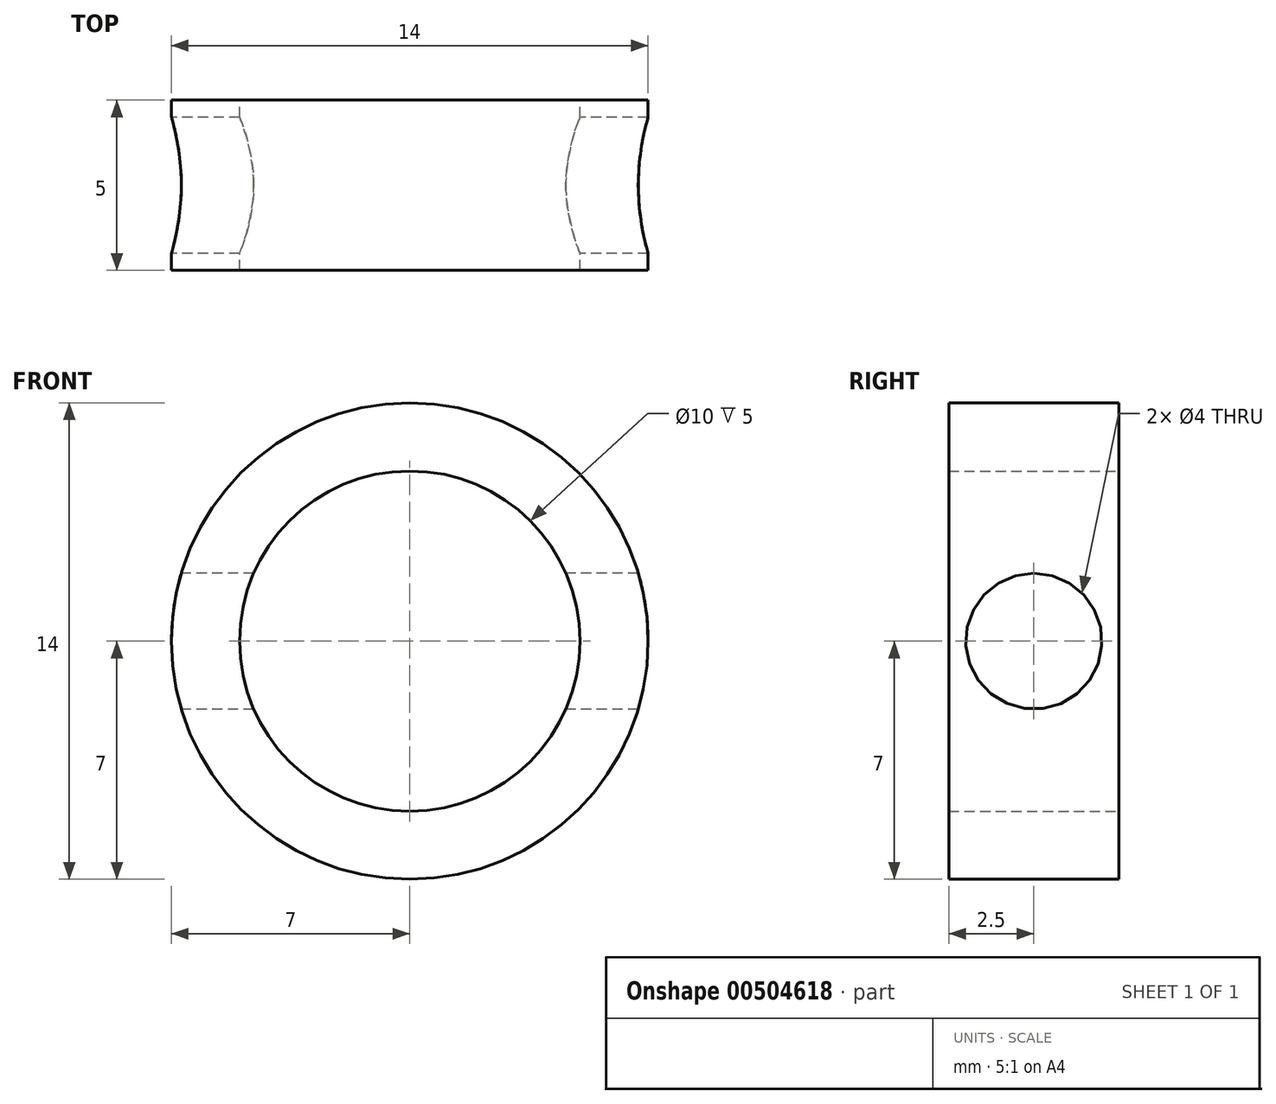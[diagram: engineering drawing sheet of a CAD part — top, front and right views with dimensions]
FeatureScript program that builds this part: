
annotation { "Feature Type Name" : "Feature", "Feature Type Description" : "" }
export const myFeature = defineFeature(function(context is Context, id is Id, definition is map)
    precondition{}
    {
        {
            var Q0;
            Q0=qCreatedBy(makeId("Front.planeOp"),FACE);
            var sketch = newSketch(context, id + "F0", { "sketchPlane" : qUnion([Q0])});
            skCircle(sketch, "E0", {"center": v(0, 0) * mm, "radius": 5 * mm});
            skCircle(sketch, "E1", {"center": v(0, 0) * mm, "radius": 7 * mm});
            skSolve(sketch);
        }
        {
            var Q0;
            Q0 = qSketchRegion(id + "F0", true);
            extrude(context, id + "F1", {"entities" : qUnion([Q0]), "depth" : 5 * mm, "offsetDistance" : 25 * mm});
        }
        {
            var Q0;
            Q0=qCreatedBy(makeId("Right.planeOp"),FACE);
            var sketch = newSketch(context, id + "F2", { "sketchPlane" : qUnion([Q0])});
            skCircle(sketch, "E2", {"center": v(-2.5, 0) * mm, "radius": 2 * mm});
            skSolve(sketch);
        }
        {
            var Q0;
            Q0 = qSketchRegion(id + "F2", true);
            extrude(context, id + "F3", {"entities" : qUnion([Q0]), "operationType" : NewBodyOperationType.REMOVE, "depth" : 10 * mm, "offsetDistance" : 25 * mm, "hasSecondDirection" : true, "secondDirectionOppositeDirection" : true, "secondDirectionDepth" : 10 * mm});
        }
    });
